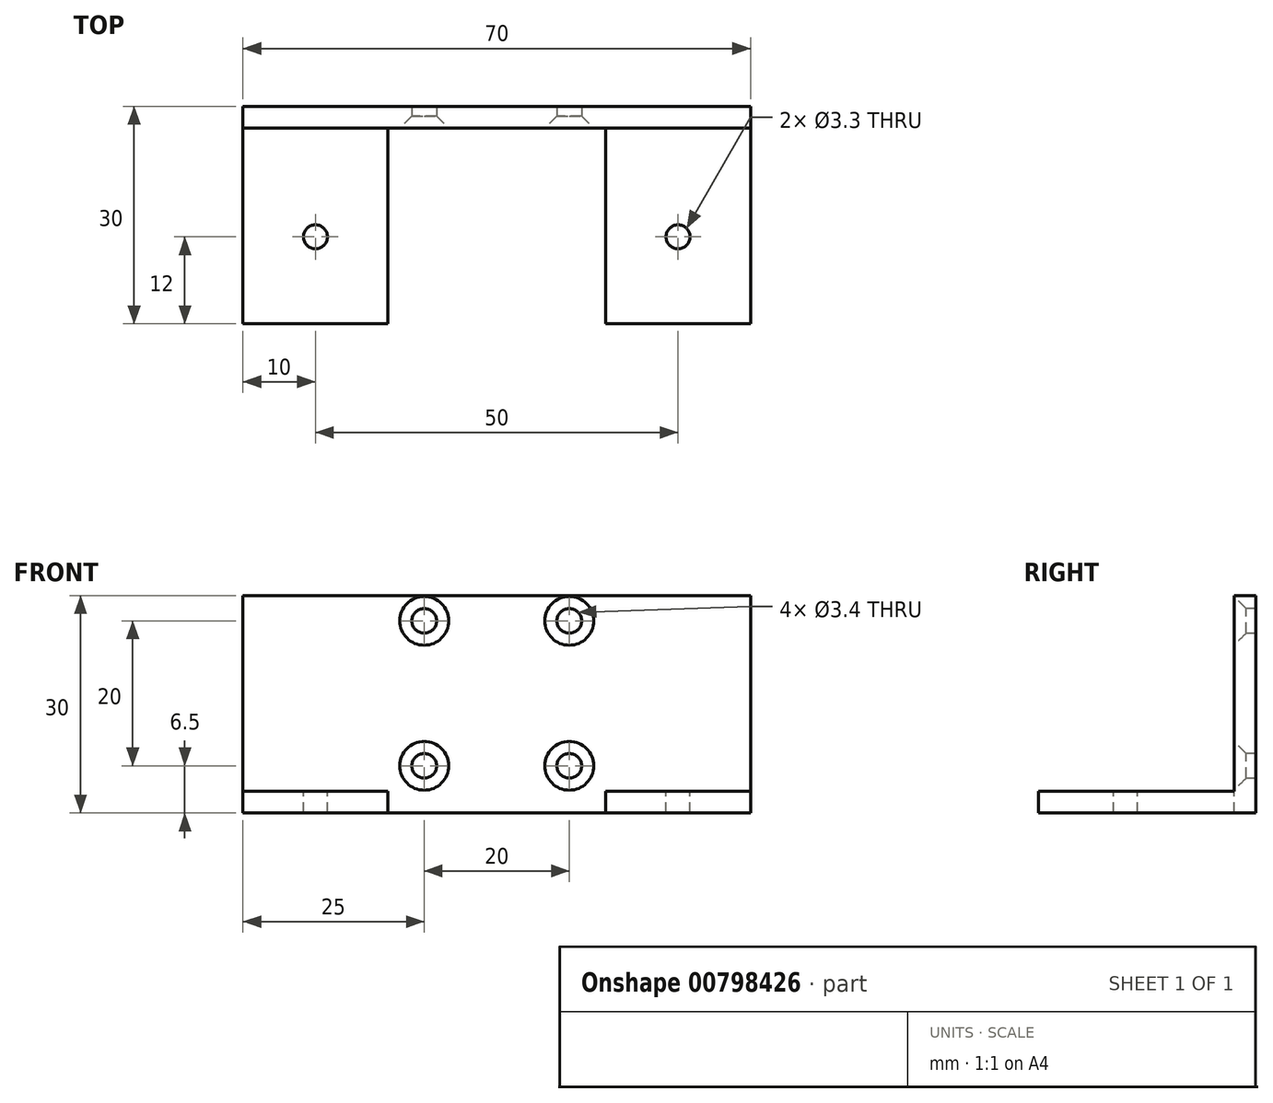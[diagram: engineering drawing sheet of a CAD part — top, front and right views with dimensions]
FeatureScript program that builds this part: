
annotation { "Feature Type Name" : "Feature", "Feature Type Description" : "" }
export const myFeature = defineFeature(function(context is Context, id is Id, definition is map)
    precondition{}
    {
        {
            var Q0;
            Q0=qCreatedBy(makeId("Front.planeOp"),FACE);
            var sketch = newSketch(context, id + "F0", { "sketchPlane" : qUnion([Q0])});
            skLineSegment(sketch, "E0.bottom", {"start": v(0, 0) * mm, "end": v(50, 0) * mm});
            skLineSegment(sketch, "E0.top", {"start": v(0, 30) * mm, "end": v(50, 30) * mm});
            skLineSegment(sketch, "E0.left", {"start": v(0, 0) * mm, "end": v(0, 30) * mm});
            skLineSegment(sketch, "E0.right", {"start": v(50, 0) * mm, "end": v(50, 30) * mm});
            skLineSegment(sketch, "E1", {"start": v(0, 3) * mm, "end": v(50, 3) * mm});
            skLineSegment(sketch, "E2", {"start": v(25, 30) * mm, "end": v(25, 3) * mm, "construction": true});
            skLineSegment(sketch, "E3", {"start": v(50, 26.5) * mm, "end": v(0, 26.5) * mm, "construction": true});
            skLineSegment(sketch, "E4", {"start": v(50, 6.5) * mm, "end": v(0, 6.5) * mm, "construction": true});
            skLineSegment(sketch, "E5", {"start": v(35, 30) * mm, "end": v(35, 3) * mm, "construction": true});
            skLineSegment(sketch, "E6", {"start": v(15, 30) * mm, "end": v(15, 3) * mm, "construction": true});
            skPoint(sketch, "E7", {"position": v(35, 26.5) * mm});
            skPoint(sketch, "E8", {"position": v(15, 26.5) * mm});
            skPoint(sketch, "E9", {"position": v(15, 6.5) * mm});
            skPoint(sketch, "E10", {"position": v(35, 6.5) * mm});
            skLineSegment(sketch, "E11", {"start": v(5, 30) * mm, "end": v(5, 3) * mm, "construction": true});
            skLineSegment(sketch, "E12", {"start": v(45, 30) * mm, "end": v(45, 3) * mm, "construction": true});
            skLineSegment(sketch, "E13", {"start": v(0, 16.5) * mm, "end": v(50, 16.5) * mm, "construction": true});
            skPoint(sketch, "E14", {"position": v(45, 16.5) * mm});
            skPoint(sketch, "E15", {"position": v(5, 16.5) * mm});
            skSolve(sketch);
        }
        {
            var Q0;
            {var subQ0=sQuery(id+"F0.wireOp",EDGE,"E0.top");Q0=makeQuery(id+"F0.imprint","IMPRINT",FACE,{"disambiguationData":[TD([[makeQuery(id+"F0.imprint","IMPRINT",EDGE,{"derivedFrom":subQ0}),-1.0]])]});}
            extrude(context, id + "F1", {"entities" : qUnion([Q0]), "oppositeDirection" : true, "depth" : 3 * mm, "offsetDistance" : 25 * mm});
        }
        {
            var Q0;
            Q0=sQuery(id+"F0.wireOp",VERTEX,"E7");
            var Q1;
            Q1=sQuery(id+"F0.wireOp",VERTEX,"E8");
            var Q2;
            Q2=sQuery(id+"F0.wireOp",VERTEX,"E9");
            var Q3;
            Q3=sQuery(id+"F0.wireOp",VERTEX,"E10");
            var Q4;
            Q4=makeQuery(id+"F1.opExtrude","SWEPT_BODY",BODY,{"disambiguationData":[OSD([sQuery(id+"F0.wireOp",EDGE,"E0.top"),sQuery(id+"F0.wireOp",EDGE,"E0.left"),sQuery(id+"F0.wireOp",EDGE,"E0.right"),sQuery(id+"F0.wireOp",EDGE,"E1")])]});
            hole(context, id + "F2", {"style" : HoleStyle.C_SINK, "endStyle" : HoleEndStyle.BLIND, "standardTappedOrClearance" : lookupTablePath({ "fit" : "Normal", "standard" : "ISO", "size" : "M3", "type" : "Clearance" }), "standardBlindInLast" : lookupTablePath({ "fit" : "Normal", "standard" : "ISO", "size" : "M3", "type" : "Clearance" }), "holeDiameter" : 3.4 * mm, "cSinkDiameter" : 6.72 * mm, "cSinkAngle" : 90 * degree, "majorDiameter" : 5 * mm, "holeDepth" : 5 * mm, "tappedDepth" : 12 * mm, "tapClearance" : 3, "locations" : qUnion([Q0, Q1, Q2, Q3]), "scope" : qUnion([Q4])});
        }
        {
            var Q0;
            Q0=makeQuery(id+"F1.opExtrude","SWEPT_FACE",FACE,{"disambiguationData":[OSD([sQuery(id+"F0.wireOp",EDGE,"E1")])]});
            extrude(context, id + "F3", {"entities" : qUnion([Q0]), "operationType" : NewBodyOperationType.ADD, "depth" : 3 * mm, "offsetDistance" : 25 * mm});
        }
        {
            var Q0;
            {var subQ0=sQuery(id+"F0.wireOp",EDGE,"E0.bottom");Q0=makeQuery(id+"F0.imprint","IMPRINT",FACE,{"disambiguationData":[TD([[makeQuery(id+"F0.imprint","IMPRINT",EDGE,{"derivedFrom":subQ0}),1.0]])]});}
            extrude(context, id + "F4", {"entities" : qUnion([Q0]), "operationType" : NewBodyOperationType.ADD, "depth" : 27 * mm, "offsetDistance" : 25 * mm});
        }
        {
            var Q0;
            {var subQ0=sQuery(id+"F0.wireOp",EDGE,"E0.right");Q0=makeQuery(id+"F4.boolean.opBoolean","MERGE",FACE,{"derivedFrom":[makeQuery(id+"F3.boolean.opBoolean","MERGE",FACE,{"derivedFrom":[makeQuery(id+"F1.opExtrude","SWEPT_FACE",FACE,{"disambiguationData":[OSD([subQ0])]}),makeQuery(id+"F3.opExtrude","SWEPT_FACE",FACE,{"disambiguationData":[OSD([subQ0,sQuery(id+"F0.wireOp",EDGE,"E1")])]})]}),makeQuery(id+"F4.opExtrude","SWEPT_FACE",FACE,{"disambiguationData":[OSD([subQ0])]})]});}
            extrude(context, id + "F5", {"entities" : qUnion([Q0]), "operationType" : NewBodyOperationType.ADD, "depth" : 10 * mm, "offsetDistance" : 25 * mm});
        }
        {
            var Q0;
            {var subQ0=sQuery(id+"F0.wireOp",EDGE,"E0.left");Q0=makeQuery(id+"F4.boolean.opBoolean","MERGE",FACE,{"derivedFrom":[makeQuery(id+"F3.boolean.opBoolean","MERGE",FACE,{"derivedFrom":[makeQuery(id+"F1.opExtrude","SWEPT_FACE",FACE,{"disambiguationData":[OSD([subQ0])]}),makeQuery(id+"F3.opExtrude","SWEPT_FACE",FACE,{"disambiguationData":[OSD([subQ0,sQuery(id+"F0.wireOp",EDGE,"E1")])]})]}),makeQuery(id+"F4.opExtrude","SWEPT_FACE",FACE,{"disambiguationData":[OSD([subQ0])]})]});}
            extrude(context, id + "F6", {"entities" : qUnion([Q0]), "operationType" : NewBodyOperationType.ADD, "depth" : 10 * mm, "offsetDistance" : 25 * mm});
        }
        {
            var Q0;
            {var subQ0=sQuery(id+"F0.wireOp",EDGE,"E1");var subQ1=sQuery(id+"F0.wireOp",EDGE,"E0.left");var subQ2=sQuery(id+"F0.wireOp",EDGE,"E0.right");Q0=makeQuery(id+"F6.boolean.opBoolean","MERGE",FACE,{"derivedFrom":[makeQuery(id+"F5.boolean.opBoolean","MERGE",FACE,{"derivedFrom":[makeQuery(id+"F4.opExtrude","SWEPT_FACE",FACE,{"disambiguationData":[OSD([subQ0])]}),makeQuery(id+"F5.opExtrude","SWEPT_FACE",FACE,{"disambiguationData":[OSD([subQ2,subQ0]),TDD([makeQuery(id+"F4.opExtrude","SWEPT_EDGE",EDGE,{"disambiguationData":[OSD([subQ2,subQ0])]})])]})]}),makeQuery(id+"F6.opExtrude","SWEPT_FACE",FACE,{"disambiguationData":[OSD([subQ1,subQ0]),TDD([makeQuery(id+"F4.opExtrude","SWEPT_EDGE",EDGE,{"disambiguationData":[OSD([subQ1,subQ0])]})])]})]});}
            var sketch = newSketch(context, id + "F7", { "sketchPlane" : qUnion([Q0])});
            skLineSegment(sketch, "E16", {"start": v(25, -27) * mm, "end": v(25, 0) * mm, "construction": true});
            skLineSegment(sketch, "E17.0", {"start": v(50, -27) * mm, "end": v(50, 0) * mm, "construction": true});
            skLineSegment(sketch, "E18.0", {"start": v(0, -27) * mm, "end": v(0, 0) * mm, "construction": true});
            skLineSegment(sketch, "E19.0", {"start": v(40, -27) * mm, "end": v(40, 0) * mm, "construction": true});
            skLineSegment(sketch, "E20.0", {"start": v(10, -27) * mm, "end": v(10, 0) * mm, "construction": true});
            skLineSegment(sketch, "E21.bottom", {"start": v(10, 0) * mm, "end": v(40, 0) * mm});
            skLineSegment(sketch, "E21.top", {"start": v(10, -27) * mm, "end": v(40, -27) * mm});
            skLineSegment(sketch, "E21.left", {"start": v(10, 0) * mm, "end": v(10, -27) * mm});
            skLineSegment(sketch, "E21.right", {"start": v(40, 0) * mm, "end": v(40, -27) * mm});
            skPoint(sketch, "E22", {"position": v(-10, -27) * mm});
            skPoint(sketch, "E23", {"position": v(60, -27) * mm});
            skLineSegment(sketch, "E24", {"start": v(-10, -15) * mm, "end": v(60, -15) * mm, "construction": true});
            skPoint(sketch, "E25", {"position": v(0, -15) * mm});
            skPoint(sketch, "E26", {"position": v(50, -15) * mm});
            skSolve(sketch);
        }
        {
            var Q0;
            Q0=makeQuery(id+"F7.imprint","IMPRINT",FACE,{"disambiguationData":[TD([[makeQuery(id+"F7.imprint","IMPRINT",EDGE,{"derivedFrom":sQuery(id+"F7.wireOp",EDGE,"E21.bottom")}),-1.0]])]});
            extrude(context, id + "F8", {"entities" : qUnion([Q0]), "operationType" : NewBodyOperationType.REMOVE, "oppositeDirection" : true, "depth" : 7 * mm, "offsetDistance" : 25 * mm});
        }
        {
            var Q0;
            Q0=sQuery(id+"F7.wireOp",VERTEX,"E25");
            var Q1;
            Q1=sQuery(id+"F7.wireOp",VERTEX,"E26");
            var Q2;
            Q2=makeQuery(id+"F1.opExtrude","SWEPT_BODY",BODY,{"disambiguationData":[OSD([sQuery(id+"F0.wireOp",EDGE,"E0.top"),sQuery(id+"F0.wireOp",EDGE,"E0.left"),sQuery(id+"F0.wireOp",EDGE,"E0.right"),sQuery(id+"F0.wireOp",EDGE,"E1")])]});
            hole(context, id + "F9", {"style" : HoleStyle.SIMPLE, "endStyle" : HoleEndStyle.BLIND, "standardTappedOrClearance" : lookupTablePath({ "standard" : "ISO", "engagement" : "75%", "pitch" : "0.7 mm", "size" : "M4", "type" : "Tapped" }), "standardBlindInLast" : lookupTablePath({ "standard" : "ISO", "engagement" : "75%", "pitch" : "0.7 mm", "size" : "M4", "type" : "Tapped" }), "holeDiameter" : 3.3 * mm, "majorDiameter" : 4 * mm, "showTappedDepth" : true, "holeDepth" : 14.1 * mm, "tappedDepth" : 12 * mm, "tapClearance" : 3, "locations" : qUnion([Q0, Q1]), "scope" : qUnion([Q2])});
        }
    });
